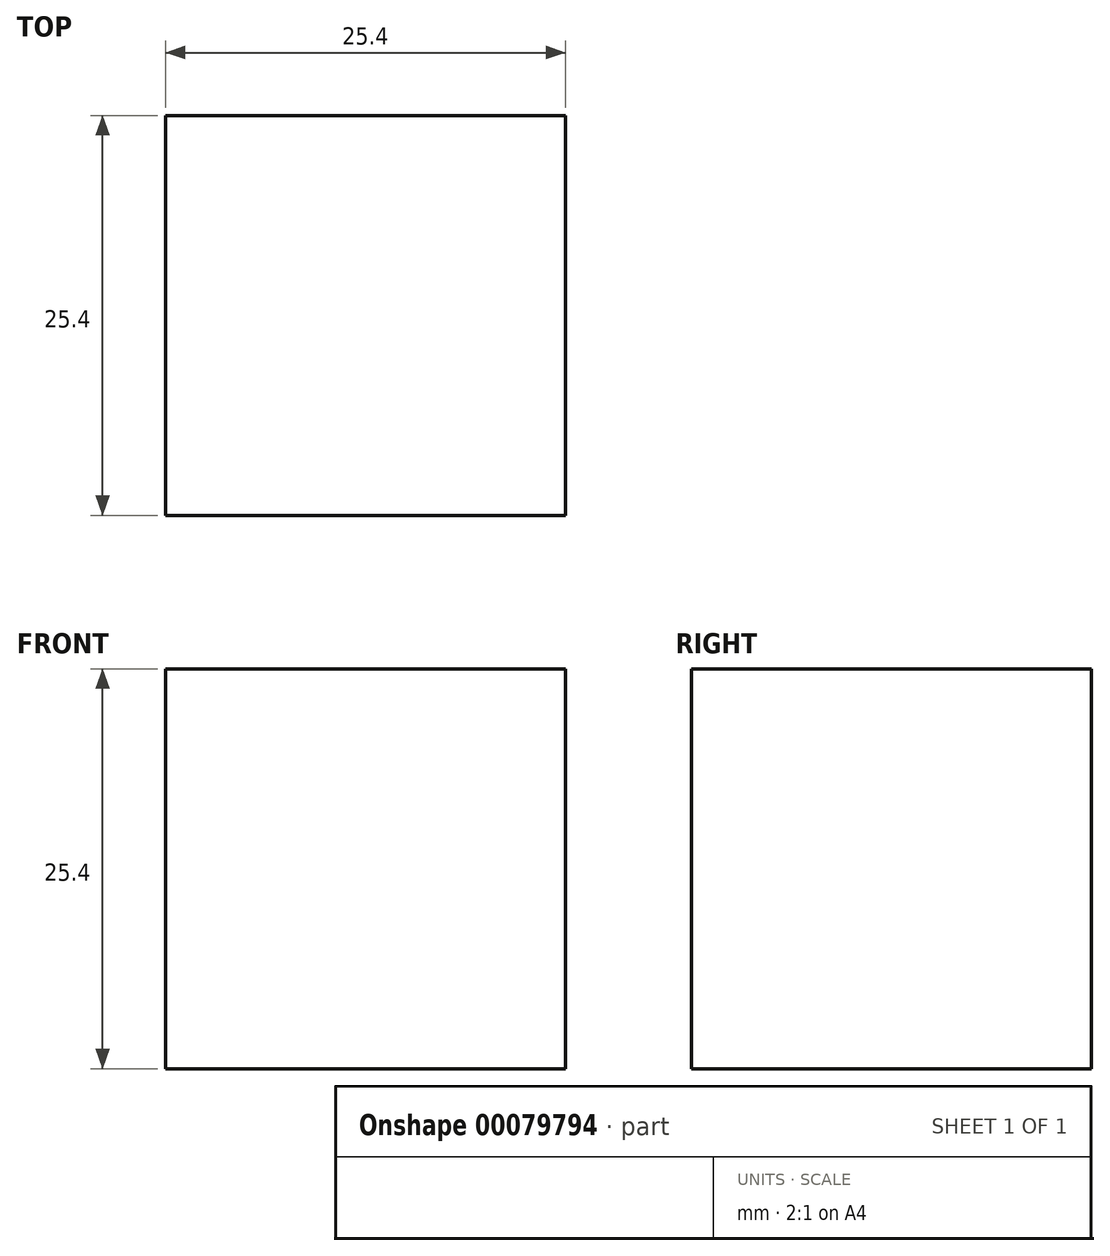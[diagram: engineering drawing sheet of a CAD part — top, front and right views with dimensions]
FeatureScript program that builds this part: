
annotation { "Feature Type Name" : "Feature", "Feature Type Description" : "" }
export const myFeature = defineFeature(function(context is Context, id is Id, definition is map)
    precondition{}
    {
        {
            var Q0;
            Q0=qCreatedBy(makeId("Front.planeOp"),FACE);
            var sketch = newSketch(context, id + "F0", { "sketchPlane" : qUnion([Q0])});
            skLineSegment(sketch, "E0.bottom", {"start": v(0, 0) * mm, "end": v(25.4, 0) * mm});
            skLineSegment(sketch, "E0.top", {"start": v(0, -25.4) * mm, "end": v(25.4, -25.4) * mm});
            skLineSegment(sketch, "E0.left", {"start": v(0, 0) * mm, "end": v(0, -25.4) * mm});
            skLineSegment(sketch, "E0.right", {"start": v(25.4, 0) * mm, "end": v(25.4, -25.4) * mm});
            skSolve(sketch);
        }
        {
            var Q0;
            Q0=makeQuery(id+"F0.imprint","IMPRINT",FACE,{"disambiguationData":[TD([[makeQuery(id+"F0.imprint","IMPRINT",EDGE,{"derivedFrom":sQuery(id+"F0.wireOp",EDGE,"E0.bottom")}),-1.0]])]});
            extrude(context, id + "F1", {"entities" : qUnion([Q0]), "oppositeDirection" : true, "depth" : 25.4 * mm});
        }
    });
